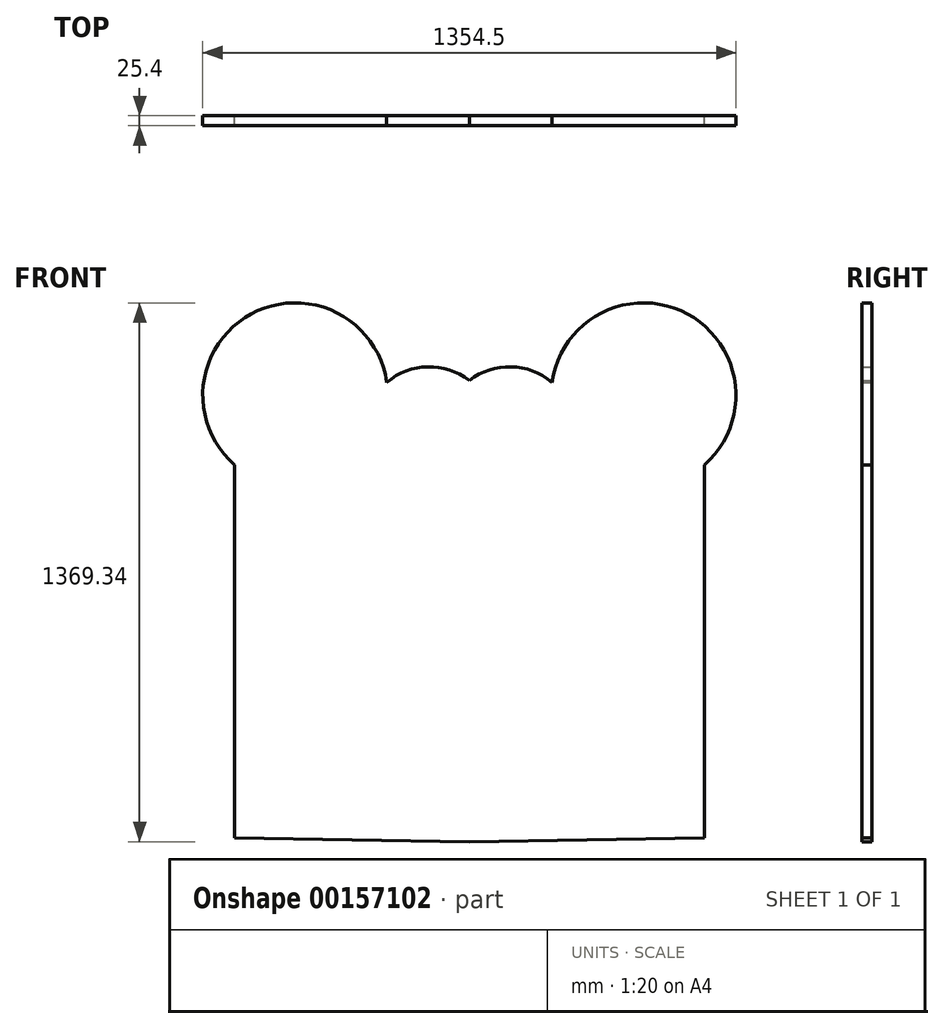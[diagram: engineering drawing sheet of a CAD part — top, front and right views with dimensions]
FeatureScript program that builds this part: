
annotation { "Feature Type Name" : "Feature", "Feature Type Description" : "" }
export const myFeature = defineFeature(function(context is Context, id is Id, definition is map)
    precondition{}
    {
        {
            var Q0;
            Q0=qCreatedBy(makeId("Front.planeOp"),FACE);
            var sketch = newSketch(context, id + "F0", { "sketchPlane" : qUnion([Q0])});
            skLineSegment(sketch, "E0", {"start": v(-596.9, -391.72) * mm, "end": v(-596.9, 512.9) * mm});
            skArc(sketch, "E1", {"start": v(-387.04, 775.74) * mm, "mid": v(-626.48, 751.72) * mm, "end": v(-596.9, 512.9) * mm});
            skArc(sketch, "E2", {"start": v(0, 565.88) * mm, "mid": v(-42.56, 949.22) * mm, "end": v(-387.04, 775.74) * mm});
            skLineSegment(sketch, "E3", {"start": v(0, 565.88) * mm, "end": v(0, -381.54) * mm});
            skLineSegment(sketch, "E4", {"start": v(0, -381.54) * mm, "end": v(-596.9, -391.72) * mm});
            skArc(sketch, "E5.MirrorCS", {"start": v(-806.76, 775.74) * mm, "mid": v(-567.32, 751.72) * mm, "end": v(-596.9, 512.9) * mm});
            skLineSegment(sketch, "E6.MirrorCS", {"start": v(-1193.8, -381.54) * mm, "end": v(-596.9, -391.72) * mm});
            skLineSegment(sketch, "E7.MirrorCS", {"start": v(-1193.8, 565.88) * mm, "end": v(-1193.8, -381.54) * mm});
            skArc(sketch, "E8.MirrorCS", {"start": v(-1193.8, 565.88) * mm, "mid": v(-1151.24, 949.22) * mm, "end": v(-806.76, 775.74) * mm});
            skSolve(sketch);
        }
        {
            var Q0;
            Q0 = qSketchRegion(id + "F0", true);
            extrude(context, id + "F1", {"entities" : qUnion([Q0]), "depth" : 25.4 * mm});
        }
    });
